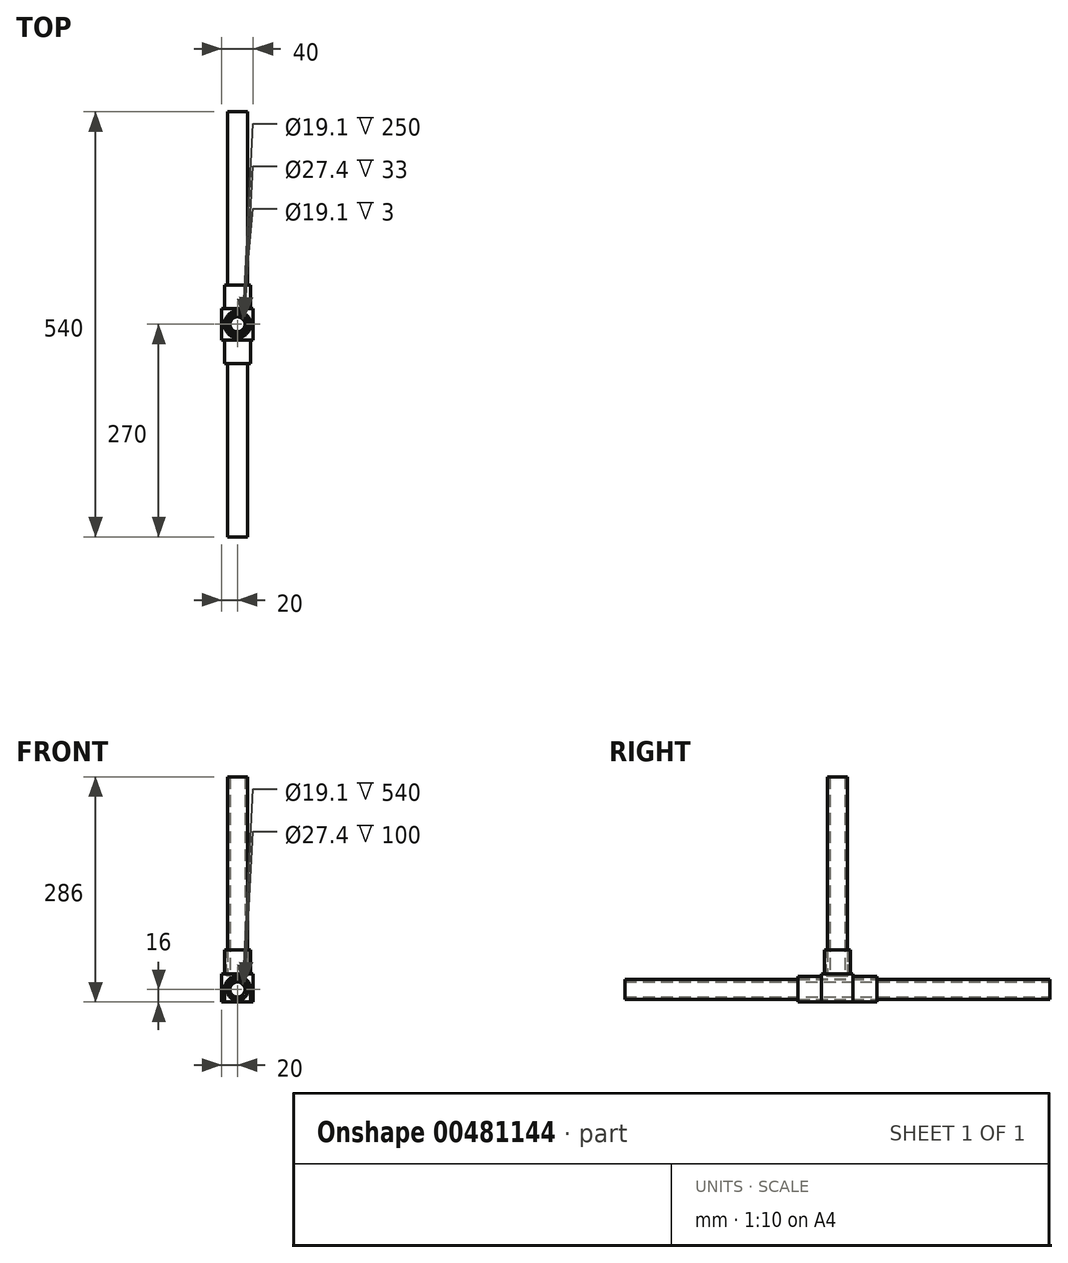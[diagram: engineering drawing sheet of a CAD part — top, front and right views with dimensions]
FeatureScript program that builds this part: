
annotation { "Feature Type Name" : "Feature", "Feature Type Description" : "" }
export const myFeature = defineFeature(function(context is Context, id is Id, definition is map)
    precondition{}
    {
        {
            var Q0;
            Q0=qCreatedBy(makeId("Front.planeOp"),FACE);
            var sketch = newSketch(context, id + "F0", { "sketchPlane" : qUnion([Q0])});
            skLineSegment(sketch, "E0.bottom", {"start": v(20, 20) * mm, "end": v(-20, 20) * mm});
            skLineSegment(sketch, "E0.top", {"start": v(20, -20) * mm, "end": v(-20, -20) * mm});
            skLineSegment(sketch, "E0.left", {"start": v(20, 20) * mm, "end": v(20, -20) * mm});
            skLineSegment(sketch, "E0.right", {"start": v(-20, 20) * mm, "end": v(-20, -20) * mm});
            skPoint(sketch, "E0.middle", {"position": v(0, 0) * mm});
            skCircle(sketch, "E1", {"center": v(0, 0) * mm, "radius": 12.7 * mm});
            skCircle(sketch, "E2.0", {"center": v(0, 0) * mm, "radius": 9.55 * mm});
            skCircle(sketch, "E3.0", {"center": v(0, 0) * mm, "radius": 13.7 * mm});
            skCircle(sketch, "E4.0", {"center": v(0, 0) * mm, "radius": 16.7 * mm});
            skSolve(sketch);
        }
        {
            var Q0;
            Q0=makeQuery(id+"F0.imprint","IMPRINT",FACE,{"disambiguationData":[TD([[makeQuery(id+"F0.imprint","IMPRINT",EDGE,{"derivedFrom":sQuery(id+"F0.wireOp",EDGE,"E0.bottom")}),1.0]])]});
            var Q1;
            Q1=makeQuery(id+"F0.imprint","IMPRINT",FACE,{"disambiguationData":[TD([[makeQuery(id+"F0.imprint","IMPRINT",EDGE,{"derivedFrom":sQuery(id+"F0.wireOp",EDGE,"E1")}),1.0]])]});
            var Q2;
            Q2=makeQuery(id+"F0.imprint","IMPRINT",FACE,{"disambiguationData":[TD([[makeQuery(id+"F0.imprint","IMPRINT",EDGE,{"derivedFrom":sQuery(id+"F0.wireOp",EDGE,"E3.0")}),-1.0]])]});
            extrude(context, id + "F1", {"entities" : qUnion([Q0, Q1, Q2]), "endBound" : BoundingType.SYMMETRIC, "depth" : 40 * mm});
        }
        {
            var Q0;
            Q0=makeQuery(id+"F1.opExtrude","CAP_FACE",FACE,{"disambiguationData":[OSD([sQuery(id+"F0.wireOp",EDGE,"E0.bottom"),sQuery(id+"F0.wireOp",EDGE,"E0.top"),sQuery(id+"F0.wireOp",EDGE,"E0.left"),sQuery(id+"F0.wireOp",EDGE,"E0.right"),sQuery(id+"F0.wireOp",EDGE,"E3.0")])],"isStart":false});
            var sketch = newSketch(context, id + "F2", { "sketchPlane" : qUnion([Q0])});
            skCircle(sketch, "E5.0", {"center": v(0, 0) * mm, "radius": 16.7 * mm});
            skSolve(sketch);
        }
        {
            var Q0;
            Q0=makeQuery(id+"F1.opExtrude","CAP_FACE",FACE,{"disambiguationData":[OSD([sQuery(id+"F0.wireOp",EDGE,"E0.bottom"),sQuery(id+"F0.wireOp",EDGE,"E0.top"),sQuery(id+"F0.wireOp",EDGE,"E0.left"),sQuery(id+"F0.wireOp",EDGE,"E0.right"),sQuery(id+"F0.wireOp",EDGE,"E3.0")])],"isStart":true});
            var sketch = newSketch(context, id + "F3", { "sketchPlane" : qUnion([Q0])});
            skCircle(sketch, "E6.0", {"center": v(0, 0) * mm, "radius": 16.7 * mm});
            skSolve(sketch);
        }
        {
            var Q0;
            Q0=makeQuery(id+"F2.imprint","IMPRINT",FACE,{"disambiguationData":[TD([[makeQuery(id+"F2.imprint","IMPRINT",EDGE,{"derivedFrom":sQuery(id+"F2.wireOp",EDGE,"E5.0")}),1.0]])]});
            var Q1;
            Q1=makeQuery(id+"F3.imprint","IMPRINT",FACE,{"disambiguationData":[TD([[makeQuery(id+"F3.imprint","IMPRINT",EDGE,{"derivedFrom":sQuery(id+"F3.wireOp",EDGE,"E6.0")}),1.0]])]});
            extrude(context, id + "F4", {"entities" : qUnion([Q0, Q1]), "operationType" : NewBodyOperationType.ADD, "endBound" : BoundingType.SYMMETRIC, "depth" : 60 * mm});
        }
        {
            var Q0;
            Q0=makeQuery(id+"F1.opExtrude","CAP_FACE",FACE,{"disambiguationData":[OSD([sQuery(id+"F0.wireOp",EDGE,"E1"),sQuery(id+"F0.wireOp",EDGE,"E2.0")])],"isStart":false});
            var Q1;
            Q1=makeQuery(id+"F1.opExtrude","CAP_FACE",FACE,{"disambiguationData":[OSD([sQuery(id+"F0.wireOp",EDGE,"E1"),sQuery(id+"F0.wireOp",EDGE,"E2.0")])],"isStart":true});
            extrude(context, id + "F5", {"entities" : qUnion([Q0, Q1]), "operationType" : NewBodyOperationType.ADD, "endBound" : BoundingType.SYMMETRIC, "depth" : 500 * mm});
        }
        {
            var Q0;
            Q0=makeQuery(id+"F1.opExtrude","SWEPT_FACE",FACE,{"disambiguationData":[OSD([sQuery(id+"F0.wireOp",EDGE,"E0.bottom")])]});
            var sketch = newSketch(context, id + "F6", { "sketchPlane" : qUnion([Q0])});
            skLineSegment(sketch, "E7.bottom", {"start": v(20, 20) * mm, "end": v(-20, 20) * mm});
            skLineSegment(sketch, "E7.top", {"start": v(20, -20) * mm, "end": v(-20, -20) * mm});
            skLineSegment(sketch, "E7.left", {"start": v(20, 20) * mm, "end": v(20, -20) * mm});
            skLineSegment(sketch, "E7.right", {"start": v(-20, 20) * mm, "end": v(-20, -20) * mm});
            skPoint(sketch, "E7.middle", {"position": v(0, 0) * mm});
            skCircle(sketch, "E8", {"center": v(0, 0) * mm, "radius": 12.7 * mm});
            skCircle(sketch, "E9.0", {"center": v(0, 0) * mm, "radius": 9.55 * mm});
            skCircle(sketch, "E10.0", {"center": v(0, 0) * mm, "radius": 13.7 * mm});
            skCircle(sketch, "E11.0", {"center": v(0, 0) * mm, "radius": 16.7 * mm});
            skSolve(sketch);
        }
        {
            var Q0;
            Q0=makeQuery(id+"F6.imprint","IMPRINT",FACE,{"disambiguationData":[TD([[makeQuery(id+"F6.imprint","IMPRINT",EDGE,{"derivedFrom":sQuery(id+"F6.wireOp",EDGE,"E8")}),-1.0]])]});
            var Q1;
            Q1=makeQuery(id+"F6.imprint","IMPRINT",FACE,{"disambiguationData":[TD([[makeQuery(id+"F6.imprint","IMPRINT",EDGE,{"derivedFrom":sQuery(id+"F6.wireOp",EDGE,"E8")}),1.0]])]});
            var Q2;
            Q2=makeQuery(id+"F6.imprint","IMPRINT",FACE,{"disambiguationData":[TD([[makeQuery(id+"F6.imprint","IMPRINT",EDGE,{"derivedFrom":sQuery(id+"F6.wireOp",EDGE,"E9.0")}),1.0]])]});
            extrude(context, id + "F7", {"entities" : qUnion([Q0, Q1, Q2]), "operationType" : NewBodyOperationType.REMOVE, "oppositeDirection" : true, "depth" : 3 * mm});
        }
        {
            var Q0;
            Q0=makeQuery(id+"F6.imprint","IMPRINT",FACE,{"disambiguationData":[TD([[makeQuery(id+"F6.imprint","IMPRINT",EDGE,{"derivedFrom":sQuery(id+"F6.wireOp",EDGE,"E8")}),1.0]])]});
            extrude(context, id + "F8", {"entities" : qUnion([Q0]), "depth" : 250 * mm});
        }
        {
            var Q0;
            Q0=makeQuery(id+"F6.imprint","IMPRINT",FACE,{"disambiguationData":[TD([[makeQuery(id+"F6.imprint","IMPRINT",EDGE,{"derivedFrom":sQuery(id+"F6.wireOp",EDGE,"E10.0")}),-1.0]])]});
            extrude(context, id + "F9", {"entities" : qUnion([Q0]), "operationType" : NewBodyOperationType.ADD, "depth" : 30 * mm});
        }
        {
            var Q0;
            Q0=makeQuery(id+"F6.imprint","IMPRINT",FACE,{"disambiguationData":[TD([[makeQuery(id+"F6.imprint","IMPRINT",EDGE,{"derivedFrom":sQuery(id+"F6.wireOp",EDGE,"E8")}),1.0]])]});
            extrude(context, id + "F10", {"entities" : qUnion([Q0]), "oppositeDirection" : true, "depth" : 3 * mm});
        }
        {
            var Q0;
            Q0=makeQuery(id+"F4.opExtrude","CAP_FACE",FACE,{"disambiguationData":[OSD([sQuery(id+"F0.wireOp",EDGE,"E3.0"),sQuery(id+"F2.wireOp",EDGE,"E5.0")])],"isStart":false});
            var sketch = newSketch(context, id + "F11", { "sketchPlane" : qUnion([Q0])});
            skLineSegment(sketch, "E12", {"start": v(-16.7, 0) * mm, "end": v(-16.7, -20) * mm});
            skLineSegment(sketch, "E13", {"start": v(16.7, 0) * mm, "end": v(16.7, -20) * mm});
            skLineSegment(sketch, "E14", {"start": v(16.7, -20) * mm, "end": v(-16.7, -20) * mm});
            skSolve(sketch);
        }
        {
            var Q0;
            Q0=makeQuery(id+"F4.opExtrude","CAP_FACE",FACE,{"disambiguationData":[OSD([sQuery(id+"F0.wireOp",EDGE,"E3.0"),sQuery(id+"F3.wireOp",EDGE,"E6.0")])],"isStart":true});
            var sketch = newSketch(context, id + "F12", { "sketchPlane" : qUnion([Q0])});
            skLineSegment(sketch, "E15", {"start": v(-16.7, 0) * mm, "end": v(-16.7, -20) * mm});
            skLineSegment(sketch, "E16", {"start": v(16.7, 0) * mm, "end": v(16.7, -20) * mm});
            skLineSegment(sketch, "E17", {"start": v(16.7, -20) * mm, "end": v(-16.7, -20) * mm});
            skSolve(sketch);
        }
        {
            var Q0;
            {var subQ0=sQuery(id+"F11.wireOp",EDGE,"E12");Q0=makeQuery(id+"F11.imprint","IMPRINT",FACE,{"disambiguationData":[TD([[makeQuery(id+"F11.imprint","IMPRINT",EDGE,{"derivedFrom":subQ0}),1.0]])]});}
            extrude(context, id + "F13", {"entities" : qUnion([Q0]), "operationType" : NewBodyOperationType.ADD, "endBound" : BoundingType.UP_TO_NEXT, "oppositeDirection" : true, "depth" : 25 * mm});
        }
        {
            var Q0;
            {var subQ0=sQuery(id+"F12.wireOp",EDGE,"E15");Q0=makeQuery(id+"F12.imprint","IMPRINT",FACE,{"disambiguationData":[TD([[makeQuery(id+"F12.imprint","IMPRINT",EDGE,{"derivedFrom":subQ0}),1.0]])]});}
            extrude(context, id + "F14", {"entities" : qUnion([Q0]), "operationType" : NewBodyOperationType.ADD, "endBound" : BoundingType.UP_TO_NEXT, "oppositeDirection" : true, "depth" : 25 * mm});
        }
        {
            var Q0;
            Q0=makeQuery(id+"F14.boolean.opBoolean","MERGE",FACE,{"derivedFrom":[makeQuery(id+"F13.boolean.opBoolean","MERGE",FACE,{"derivedFrom":[makeQuery(id+"F1.opExtrude","SWEPT_FACE",FACE,{"disambiguationData":[OSD([sQuery(id+"F0.wireOp",EDGE,"E0.top")])]}),makeQuery(id+"F13.opExtrude","SWEPT_FACE",FACE,{"disambiguationData":[OSD([sQuery(id+"F11.wireOp",EDGE,"E14")])]})]}),makeQuery(id+"F14.opExtrude","SWEPT_FACE",FACE,{"disambiguationData":[OSD([sQuery(id+"F12.wireOp",EDGE,"E17")])]})]});
            extrude(context, id + "F15", {"entities" : qUnion([Q0]), "operationType" : NewBodyOperationType.REMOVE, "oppositeDirection" : true, "depth" : 4 * mm});
        }
    });
